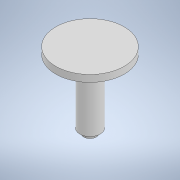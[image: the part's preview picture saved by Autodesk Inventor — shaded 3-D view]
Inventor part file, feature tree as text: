
AUTODESK INVENTOR PART (.ipt)
format: ipt  version: 2022 (Build 260153000, 153)  size: 108,544 bytes
history: native  units: in
note: dims shown in document units (in); Inventor stores cm internally (conversion verified against a paired STEP export)
features: extrude x3, sketch x3
ambient origin geometry x8: Origin, YZ Plane, XZ Plane, XY Plane, X Axis, Y Axis, Z Axis, Center Point
bodies: Solid1 (feature_tree)
feature tree (6):
  extrude  "Extrusion1"  Depth=1.1024in TaperAngle=0.0deg
  extrude  "Extrusion2"  Depth=0.0787in TaperAngle=0.0deg
  extrude  "Extrusion3"  Depth=0.1181in TaperAngle=0.0deg
  sketch  "Sketch1"  dims[d0=0.3543in d1=1.1024in d2=0.0in]
  sketch  "Sketch2"  dims[d3=0.2165in d4=0.0787in d5=0.0in]
  sketch  "Sketch3"  dims[d6=1.1811in d7=0.1181in d8=0.0in]
